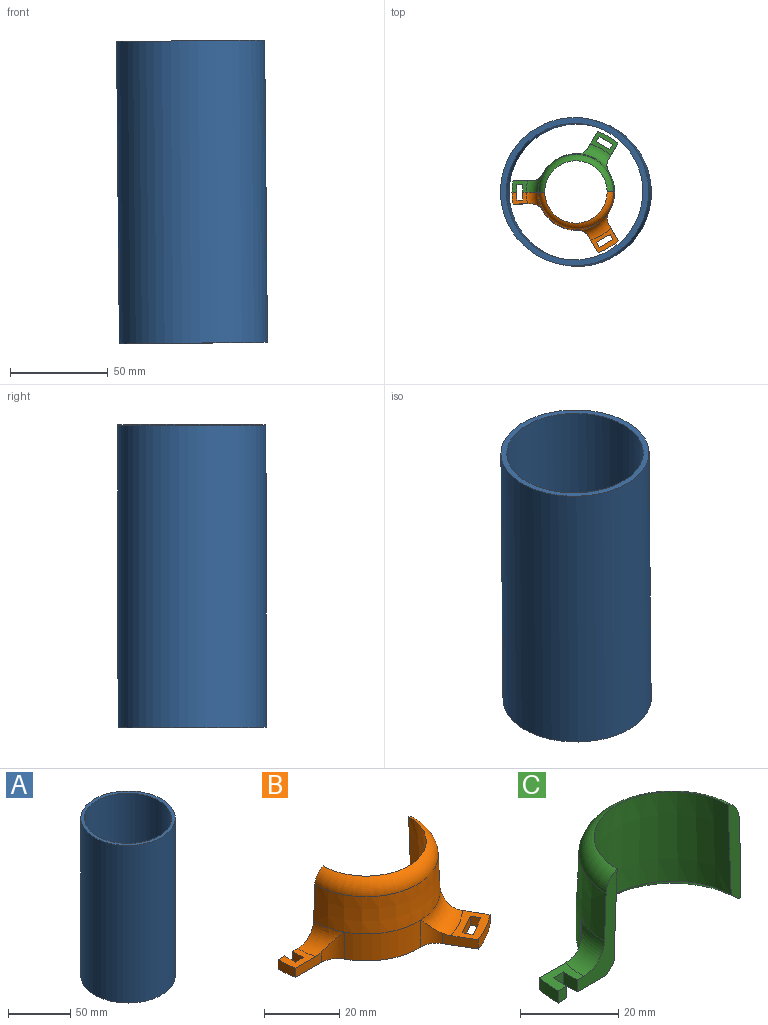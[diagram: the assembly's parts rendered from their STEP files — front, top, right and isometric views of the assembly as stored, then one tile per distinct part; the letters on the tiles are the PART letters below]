
ASSEMBLY  parts=3 mates=2
PART A: 4 faces, bbox 76x76x155 mm
  f0: cylinder r=35mm len=155mm, axis (0,0,-1), area 34086.3mm2, adj f2,f3
  f1: cylinder r=38mm len=155mm, axis (0,0,-1), area 37008mm2, adj f2,f3
  f2: plane 76x76mm, normal (0,0,1), area 688mm2, adj f0,f1
  f3: plane 76x76mm, normal (0,0,-1), area 688mm2, adj f0,f1
PART B: 29 faces, bbox 60.4x32.4x25.4 mm
  f0: cylinder r=33mm len=10.39mm, axis (0,0,-1), area 36.2mm2, adj f2,f5,f14,f20
  f1: cylinder r=33mm len=6mm, axis (0,0,-1), area 18.1mm2, adj f2,f3,f4,f13
  f2: plane 54.42x31.1mm, normal (0,0,-1), area 253.8mm2, adj f0,f1,f3,f8,f9,f13,f14,f15
  f3: plane 3x2.5mm, normal (0,1,0), area 7.5mm2, adj f1,f2,f4,f21
  f4: plane 8.06x6mm, normal (0,0,1), area 32.4mm2, adj f1,f3,f9,f11,f13,f21,f22,f23
  f5: plane 14.15x12.51mm, normal (0,0,1), area 64.9mm2, adj f0,f6,f14,f20,f24,f25,f26,f27
  f6: torus R=25.65mm, axis (0,0,-1), area 127.6mm2, adj f5,f10,f14,f15,f19,f20
  f7: cone r=17mm half-angle=2.3deg, axis (0,0,-1), area 1190.4mm2, adj f8,f9,f12,f28
  f8: plane 25x3.65mm, normal (0,1,0), area 67.9mm2, adj f2,f7,f10,f12,f18,f28
  f9: plane 25x11.5mm, normal (0,1,0), area 99.1mm2, adj f2,f4,f7,f10,f11,f12,f23,f28
  f10: cone r=19.88mm half-angle=2.3deg, axis (0,0,-1), area 719.2mm2, adj f6,f8,f9,f11,f12,f16,f18
  f11: torus R=25.65mm, axis (0,0,-1), area 63.8mm2, adj f4,f9,f10,f13,f17
  f12: torus R=14.18mm, axis (0,0,1), area 328.3mm2, adj f7,f8,f9,f10
  f13: plane 9.8x3.44mm, normal (0,-1,0), area 29.6mm2, adj f1,f2,f4,f11,f17
  f14: plane 8.49x4.91mm, normal (-0.87,-0.5,0), area 29.6mm2, adj f0,f2,f5,f6,f15
  f15: cylinder r=6mm len=8.76mm, axis (0,0,-1), area 37.4mm2, adj f2,f6,f14,f16
  f16: cylinder r=19.65mm len=18.09mm, axis (0,0,-1), area 193mm2, adj f2,f10,f15,f17
  f17: cylinder r=6mm len=8.76mm, axis (0,0,-1), area 37.4mm2, adj f2,f11,f13,f16
  f18: cylinder r=19.65mm len=10.45mm, axis (0,0,-1), area 96.5mm2, adj f2,f8,f10,f19
  f19: cylinder r=6mm len=8.76mm, axis (0,0,-1), area 37.4mm2, adj f2,f6,f18,f20
  f20: plane 8.48x4.91mm, normal (0.87,0.5,0), area 29.6mm2, adj f0,f2,f5,f6,f19
  f21: plane 4x3mm, normal (1,0,0), area 12mm2, adj f2,f3,f4,f22
  f22: plane 3x3mm, normal (0,1,0), area 9mm2, adj f2,f4,f21,f23
  f23: plane 4x3mm, normal (-1,0,0), area 12mm2, adj f2,f4,f9,f22
  f24: plane 3x2.6mm, normal (0.87,0.5,0), area 9mm2, adj f2,f5,f25,f27
  f25: plane 6.93x4mm, normal (-0.5,0.87,0), area 24mm2, adj f2,f5,f24,f26
  f26: plane 3x2.6mm, normal (-0.87,-0.5,0), area 9mm2, adj f2,f5,f25,f27
  f27: plane 6.93x4mm, normal (0.5,-0.87,0), area 24mm2, adj f2,f5,f24,f26
  f28: cone r=19mm half-angle=46.1deg, axis (0,0,-1), area 162.7mm2, adj f2,f7,f8,f9
PART C: 29 faces, bbox 60.4x32.4x25.4 mm
  f0: cylinder r=33mm len=10.39mm, axis (0,0,-1), area 36.2mm2, adj f1,f4,f17,f18
  f1: plane 54.42x31.1mm, normal (0,0,-1), area 253.8mm2, adj f0,f2,f7,f9,f10,f13,f14,f15
  f2: plane 3x2.5mm, normal (0,-1,0), area 7.5mm2, adj f1,f3,f7,f26
  f3: plane 8.06x6mm, normal (0,0,1), area 32.4mm2, adj f2,f6,f7,f10,f13,f25,f26,f27
  f4: plane 14.15x12.51mm, normal (0,0,1), area 64.9mm2, adj f0,f5,f17,f18,f21,f22,f23,f24
  f5: torus R=25.65mm, axis (0,0,-1), area 127.6mm2, adj f4,f11,f16,f17,f18,f19
  f6: torus R=25.65mm, axis (0,0,-1), area 63.8mm2, adj f3,f10,f11,f13,f14
  f7: cylinder r=33mm len=6mm, axis (0,0,-1), area 18.1mm2, adj f1,f2,f3,f13
  f8: cone r=17mm half-angle=2.3deg, axis (0,0,-1), area 1190.4mm2, adj f9,f10,f12,f28
  f9: plane 25x3.65mm, normal (0,-1,0), area 67.9mm2, adj f1,f8,f11,f12,f20,f28
  f10: plane 25x11.5mm, normal (0,-1,0), area 99.1mm2, adj f1,f3,f6,f8,f11,f12,f27,f28
  f11: cone r=19.88mm half-angle=2.3deg, axis (0,0,-1), area 719.2mm2, adj f5,f6,f9,f10,f12,f15,f20
  f12: torus R=14.18mm, axis (0,0,1), area 328.3mm2, adj f8,f9,f10,f11
  f13: plane 9.8x3.44mm, normal (0,1,0), area 29.6mm2, adj f1,f3,f6,f7,f14
  f14: cylinder r=6mm len=8.76mm, axis (0,0,-1), area 37.4mm2, adj f1,f6,f13,f15
  f15: cylinder r=19.65mm len=18.09mm, axis (0,0,-1), area 193mm2, adj f1,f11,f14,f16
  f16: cylinder r=6mm len=8.76mm, axis (0,0,-1), area 37.4mm2, adj f1,f5,f15,f17
  f17: plane 8.49x4.91mm, normal (-0.87,0.5,0), area 29.6mm2, adj f0,f1,f4,f5,f16
  f18: plane 8.48x4.91mm, normal (0.87,-0.5,0), area 29.6mm2, adj f0,f1,f4,f5,f19
  f19: cylinder r=6mm len=8.76mm, axis (0,0,-1), area 37.4mm2, adj f1,f5,f18,f20
  f20: cylinder r=19.65mm len=10.45mm, axis (0,0,-1), area 96.5mm2, adj f1,f9,f11,f19
  f21: plane 3x2.6mm, normal (-0.87,0.5,0), area 9mm2, adj f1,f4,f22,f24
  f22: plane 6.93x4mm, normal (-0.5,-0.87,0), area 24mm2, adj f1,f4,f21,f23
  f23: plane 3x2.6mm, normal (0.87,-0.5,0), area 9mm2, adj f1,f4,f22,f24
  f24: plane 6.93x4mm, normal (0.5,0.87,0), area 24mm2, adj f1,f4,f21,f23
  f25: plane 3x3mm, normal (0,-1,0), area 9mm2, adj f1,f3,f26,f27
  f26: plane 4x3mm, normal (1,0,0), area 12mm2, adj f1,f2,f3,f25
  f27: plane 4x3mm, normal (-1,0,0), area 12mm2, adj f1,f3,f10,f25
  f28: cone r=19mm half-angle=46.1deg, axis (0,0,-1), area 162.7mm2, adj f1,f8,f9,f10
PLACE A rot(axis=(-0.07,-0.93,0.35),0.6deg) t=(-24.3,-156.43,58.4)mm
PLACE B rot(axis=(-0.07,-0.93,0.35),0.6deg) t=(-22.71,-156.55,-114.1)mm
PLACE C rot(axis=(-0.07,-0.93,0.35),0.6deg) t=(-22.71,-156.55,-114.1)mm fixed
MATE fastened C.f10 <-> B.f9  axis (0,-1,0) through (-43.62,-156.51,47.87)mm
MATE cylindrical A.f1 <-> B.f7  axis (0.01,0,-1) through (-24.3,-156.43,58.4)mm
